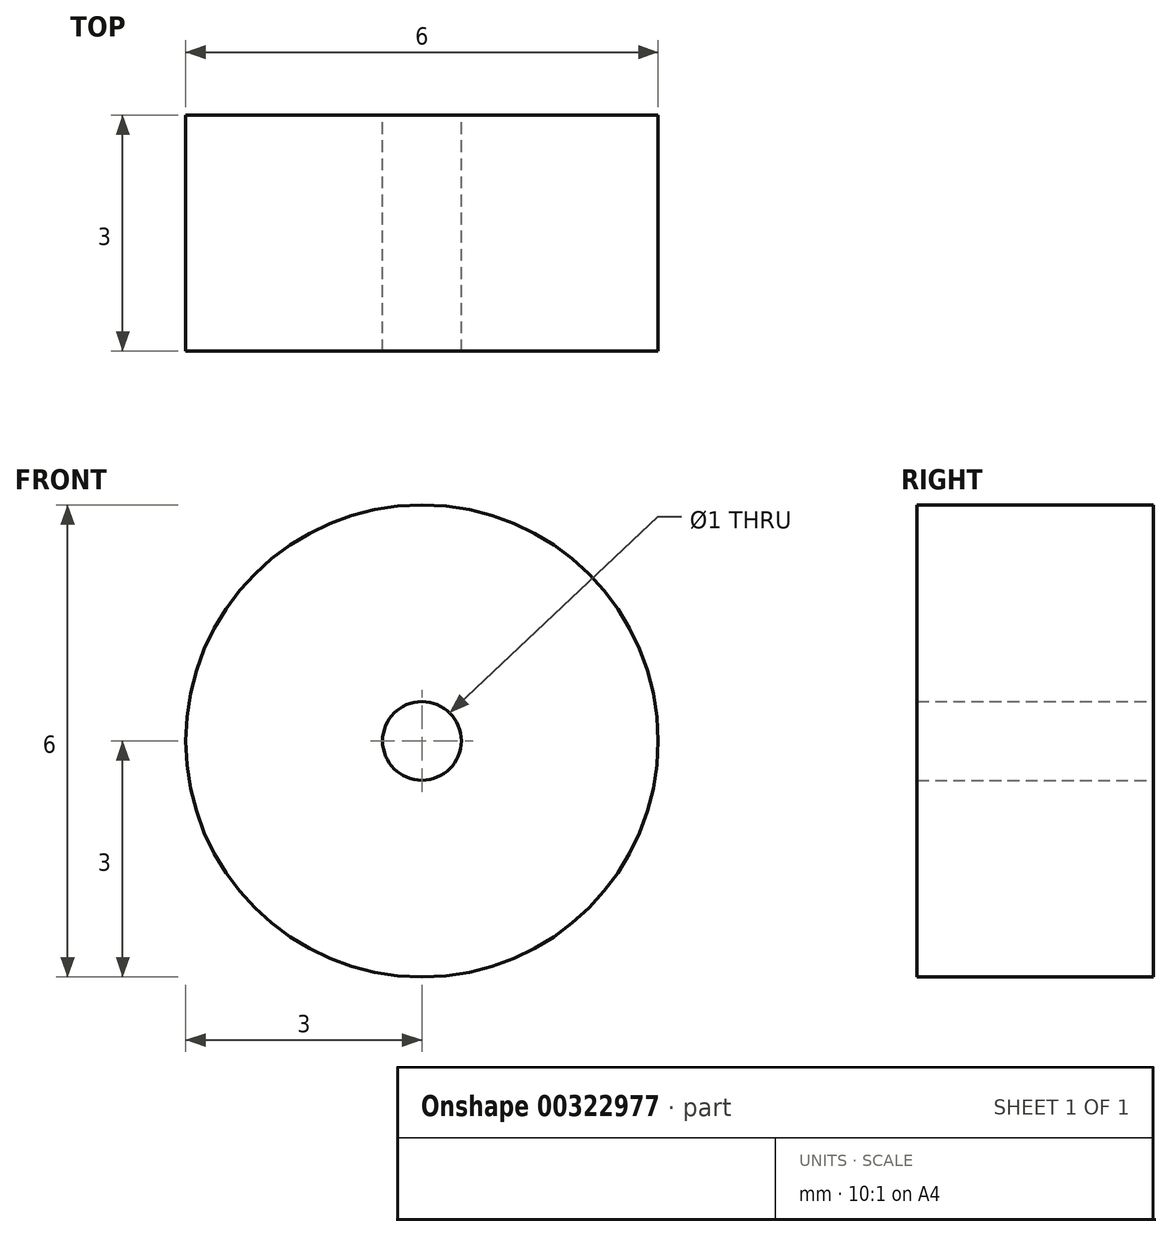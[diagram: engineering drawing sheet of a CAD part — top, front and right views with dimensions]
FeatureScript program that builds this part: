
annotation { "Feature Type Name" : "Feature", "Feature Type Description" : "" }
export const myFeature = defineFeature(function(context is Context, id is Id, definition is map)
    precondition{}
    {
        {
            var Q0;
            Q0=qCreatedBy(makeId("Front.planeOp"),FACE);
            var sketch = newSketch(context, id + "F0", { "sketchPlane" : qUnion([Q0])});
            skCircle(sketch, "E0", {"center": v(0, 0) * mm, "radius": 0.5 * mm});
            skCircle(sketch, "E1", {"center": v(0, 0) * mm, "radius": 3 * mm});
            skSolve(sketch);
        }
        {
            var Q0;
            Q0=makeQuery(id+"F0.imprint","IMPRINT",FACE,{"disambiguationData":[TD([[makeQuery(id+"F0.imprint","IMPRINT",EDGE,{"derivedFrom":sQuery(id+"F0.wireOp",EDGE,"E0")}),-1.0]])]});
            extrude(context, id + "F1", {"entities" : qUnion([Q0]), "depth" : 3 * mm});
        }
    });
